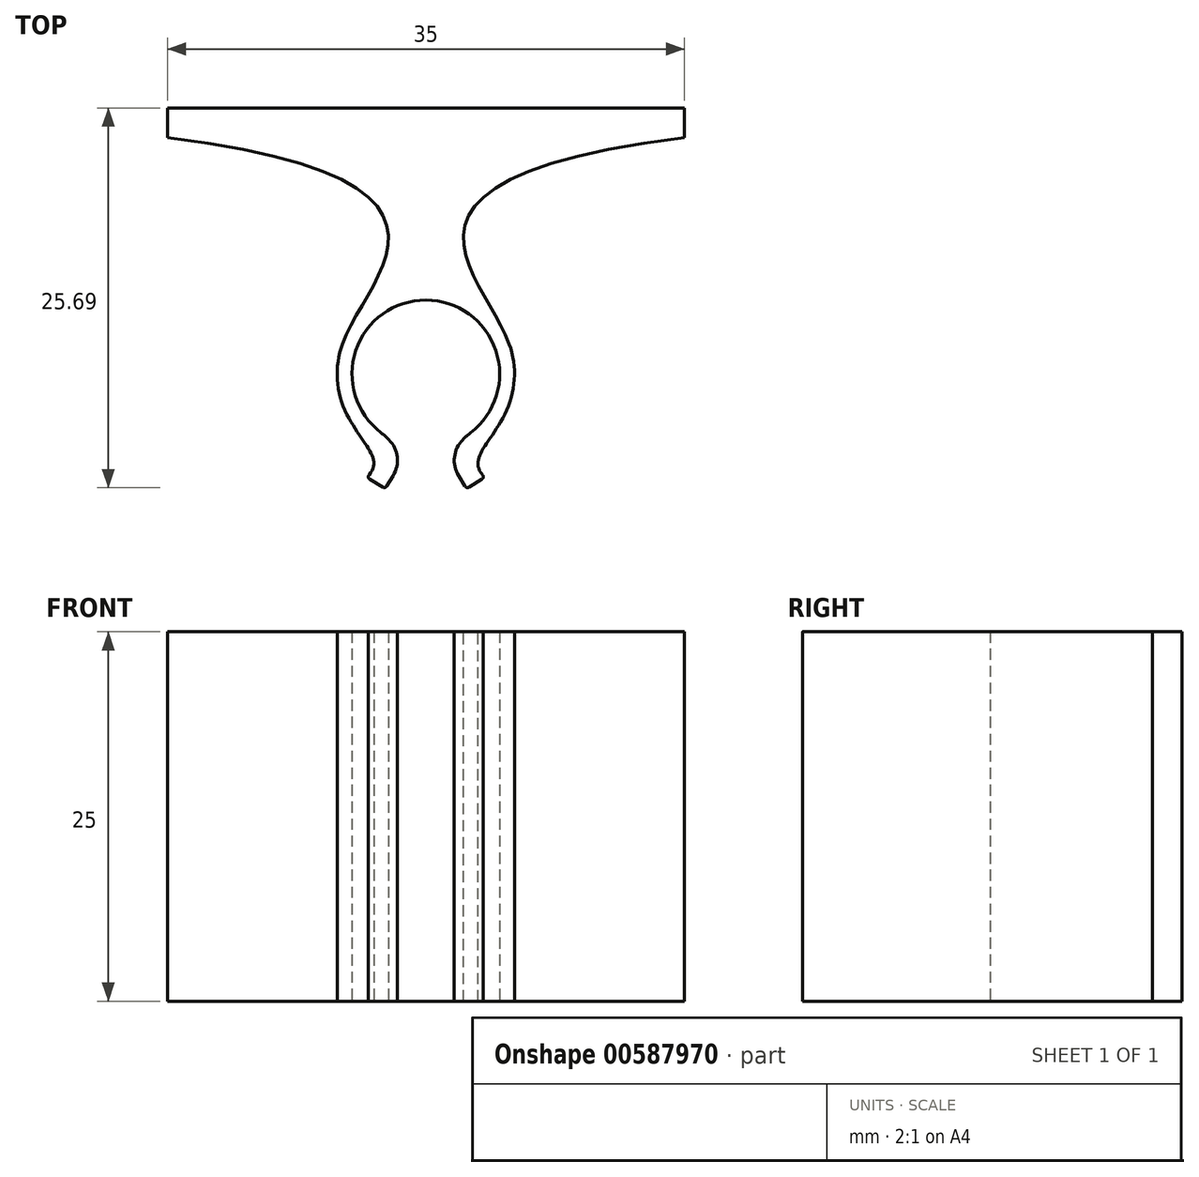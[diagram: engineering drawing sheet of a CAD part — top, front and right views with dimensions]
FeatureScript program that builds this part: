
annotation { "Feature Type Name" : "Feature", "Feature Type Description" : "" }
export const myFeature = defineFeature(function(context is Context, id is Id, definition is map)
    precondition{}
    {
        {
            var Q0;
            Q0=qCreatedBy(makeId("Top.planeOp"),FACE);
            var sketch = newSketch(context, id + "F0", { "sketchPlane" : qUnion([Q0])});
            skArc(sketch, "E0", {"start": v(1.55, -4.75) * mm, "mid": v(0, 5) * mm, "end": v(-1.55, -4.75) * mm});
            skArc(sketch, "E1", {"start": v(1.55, -5.8) * mm, "mid": v(0, 6) * mm, "end": v(-1.55, -5.8) * mm});
            skLineSegment(sketch, "E2", {"start": v(-17.5, 16) * mm, "end": v(17.5, 16) * mm});
            skLineSegment(sketch, "E3", {"start": v(0, 0) * mm, "end": v(0, 16) * mm, "construction": true});
            skLineSegment(sketch, "E4", {"start": v(-17.5, 16) * mm, "end": v(-17.5, 18) * mm});
            skLineSegment(sketch, "E5", {"start": v(-17.5, 18) * mm, "end": v(17.5, 18) * mm});
            skLineSegment(sketch, "E6", {"start": v(17.5, 18) * mm, "end": v(17.5, 16) * mm});
            skFitSpline(sketch, "E7", {"points": [v(-17.5, 16) * mm, v(-5.64, 2.04) * mm], "startDerivative": vector(66.86, -8.37) * mm, "endDerivative": vector(-5.08, -14.07) * mm});
            skFitSpline(sketch, "E8.MirrorCS", {"points": [v(17.5, 16) * mm, v(5.64, 2.04) * mm], "startDerivative": vector(-66.86, -8.37) * mm, "endDerivative": vector(5.08, -14.07) * mm});
            skFitSpline(sketch, "E9", {"points": [v(-5.35, -2.72) * mm, v(-4, -7) * mm], "startDerivative": vector(3.28, -6.45) * mm, "endDerivative": vector(-3.76, -3.7) * mm});
            skLineSegment(sketch, "E10", {"start": v(4, 0) * mm, "end": v(4, -7) * mm, "construction": true});
            skLineSegment(sketch, "E11", {"start": v(4, -7) * mm, "end": v(-4, -7) * mm, "construction": true});
            skLineSegment(sketch, "E12", {"start": v(-4, 0) * mm, "end": v(-4, -7) * mm, "construction": true});
            skLineSegment(sketch, "E13", {"start": v(-4, 0) * mm, "end": v(0, 0) * mm, "construction": true});
            skLineSegment(sketch, "E14", {"start": v(0, 0) * mm, "end": v(4, 0) * mm, "construction": true});
            skLineSegment(sketch, "E15", {"start": v(-3.8, -7.13) * mm, "end": v(-2.92, -7.66) * mm});
            skLineSegment(sketch, "E16", {"start": v(-2.65, -7.6) * mm, "end": v(-1.55, -5.8) * mm});
            skArc(sketch, "E17.filletArc", {"start": v(-3.84, -6.83) * mm, "mid": v(-3.89, -6.99) * mm, "end": v(-3.8, -7.13) * mm});
            skPoint(sketch, "E18.visualSharp", {"position": v(-2.75, -7.76) * mm});
            skArc(sketch, "E18.filletArc", {"start": v(-2.92, -7.66) * mm, "mid": v(-2.77, -7.68) * mm, "end": v(-2.65, -7.6) * mm});
            skLineSegment(sketch, "E19", {"start": v(-1.55, -5.8) * mm, "end": v(-1.55, -4.75) * mm});
            skLineSegment(sketch, "E20.MirrorCS", {"start": v(1.55, -5.8) * mm, "end": v(1.55, -4.75) * mm});
            skLineSegment(sketch, "E21.MirrorCS", {"start": v(2.65, -7.6) * mm, "end": v(1.55, -5.8) * mm});
            skArc(sketch, "E22.MirrorCS", {"start": v(2.92, -7.66) * mm, "mid": v(2.77, -7.68) * mm, "end": v(2.65, -7.6) * mm});
            skLineSegment(sketch, "E23.MirrorCS", {"start": v(3.8, -7.13) * mm, "end": v(2.92, -7.66) * mm});
            skArc(sketch, "E24.MirrorCS", {"start": v(3.84, -6.83) * mm, "mid": v(3.89, -6.99) * mm, "end": v(3.8, -7.13) * mm});
            skFitSpline(sketch, "E25.MirrorCS", {"points": [v(5.35, -2.72) * mm, v(4, -7) * mm], "startDerivative": vector(-3.28, -6.45) * mm, "endDerivative": vector(3.76, -3.7) * mm});
            skSolve(sketch);
        }
        {
            var Q0;
            Q0=makeQuery(id+"F0.imprint","IMPRINT",FACE,{"disambiguationData":[TD([[makeQuery(id+"F0.imprint","IMPRINT",EDGE,{"derivedFrom":sQuery(id+"F0.wireOp",EDGE,"E2")}),1.0]])]});
            var Q1;
            Q1=makeQuery(id+"F0.imprint","IMPRINT",FACE,{"disambiguationData":[TD([[makeQuery(id+"F0.imprint","IMPRINT",EDGE,{"derivedFrom":sQuery(id+"F0.wireOp",EDGE,"E2")}),-1.0]])]});
            var Q2;
            Q2=makeQuery(id+"F0.imprint","IMPRINT",FACE,{"disambiguationData":[TD([[makeQuery(id+"F0.imprint","IMPRINT",EDGE,{"derivedFrom":sQuery(id+"F0.wireOp",EDGE,"E0")}),-1.0]])]});
            var Q3;
            {var subQ1=sQuery(id+"F0.wireOp",EDGE,"E9");Q3=makeQuery(id+"F0.imprint","IMPRINT",FACE,{"disambiguationData":[TD([[makeQuery(id+"F0.imprint","IMPRINT",EDGE,{"derivedFrom":subQ1}),1.0]])]});}
            var Q4;
            {var subQ0=sQuery(id+"F0.wireOp",EDGE,"E21.MirrorCS");Q4=makeQuery(id+"F0.imprint","IMPRINT",FACE,{"disambiguationData":[TD([[makeQuery(id+"F0.imprint","IMPRINT",EDGE,{"derivedFrom":subQ0}),-1.0]])]});}
            extrude(context, id + "F1", {"entities" : qUnion([Q0, Q1, Q2, Q3, Q4]), "depth" : 25 * mm, "offsetDistance" : 25 * mm});
        }
        {
            var Q0;
            Q0=makeQuery(id+"F1.opExtrude","SWEPT_EDGE",EDGE,{"disambiguationData":[OSD([sQuery(id+"F0.wireOp",EDGE,"E0"),sQuery(id+"F0.wireOp",EDGE,"E19")])]});
            var Q1;
            Q1=makeQuery(id+"F1.opExtrude","SWEPT_EDGE",EDGE,{"disambiguationData":[OSD([sQuery(id+"F0.wireOp",EDGE,"E0"),sQuery(id+"F0.wireOp",EDGE,"E20.MirrorCS")])]});
            fillet(context, id + "F2", {"entities" : qUnion([Q0, Q1]), "radius" : 5 * mm, "tangentPropagation" : true, "allowEdgeOverflow" : false});
        }
        {
            var Q0;
            Q0=makeQuery(id+"F2.opFillet","BLEND_EDGE",EDGE,{"blendedFrom":[makeQuery(id+"F1.opExtrude","SWEPT_EDGE",EDGE,{"disambiguationData":[OSD([sQuery(id+"F0.wireOp",EDGE,"E0"),sQuery(id+"F0.wireOp",EDGE,"E19")])]}),makeQuery(id+"F1.opExtrude","SWEPT_FACE",FACE,{"disambiguationData":[OSD([sQuery(id+"F0.wireOp",EDGE,"E16")])]})],"blendedInto":[makeQuery(id+"F1.opExtrude","SWEPT_FACE",FACE,{"disambiguationData":[OSD([sQuery(id+"F0.wireOp",EDGE,"E16")])]})]});
            var Q1;
            Q1=makeQuery(id+"F2.opFillet","BLEND_EDGE",EDGE,{"blendedFrom":[makeQuery(id+"F1.opExtrude","SWEPT_EDGE",EDGE,{"disambiguationData":[OSD([sQuery(id+"F0.wireOp",EDGE,"E0"),sQuery(id+"F0.wireOp",EDGE,"E20.MirrorCS")])]}),makeQuery(id+"F1.opExtrude","SWEPT_FACE",FACE,{"disambiguationData":[OSD([sQuery(id+"F0.wireOp",EDGE,"E21.MirrorCS")])]})],"blendedInto":[makeQuery(id+"F1.opExtrude","SWEPT_FACE",FACE,{"disambiguationData":[OSD([sQuery(id+"F0.wireOp",EDGE,"E21.MirrorCS")])]})]});
            fillet(context, id + "F3", {"entities" : qUnion([Q0, Q1]), "radius" : 2 * mm, "tangentPropagation" : true, "allowEdgeOverflow" : false});
        }
    });
